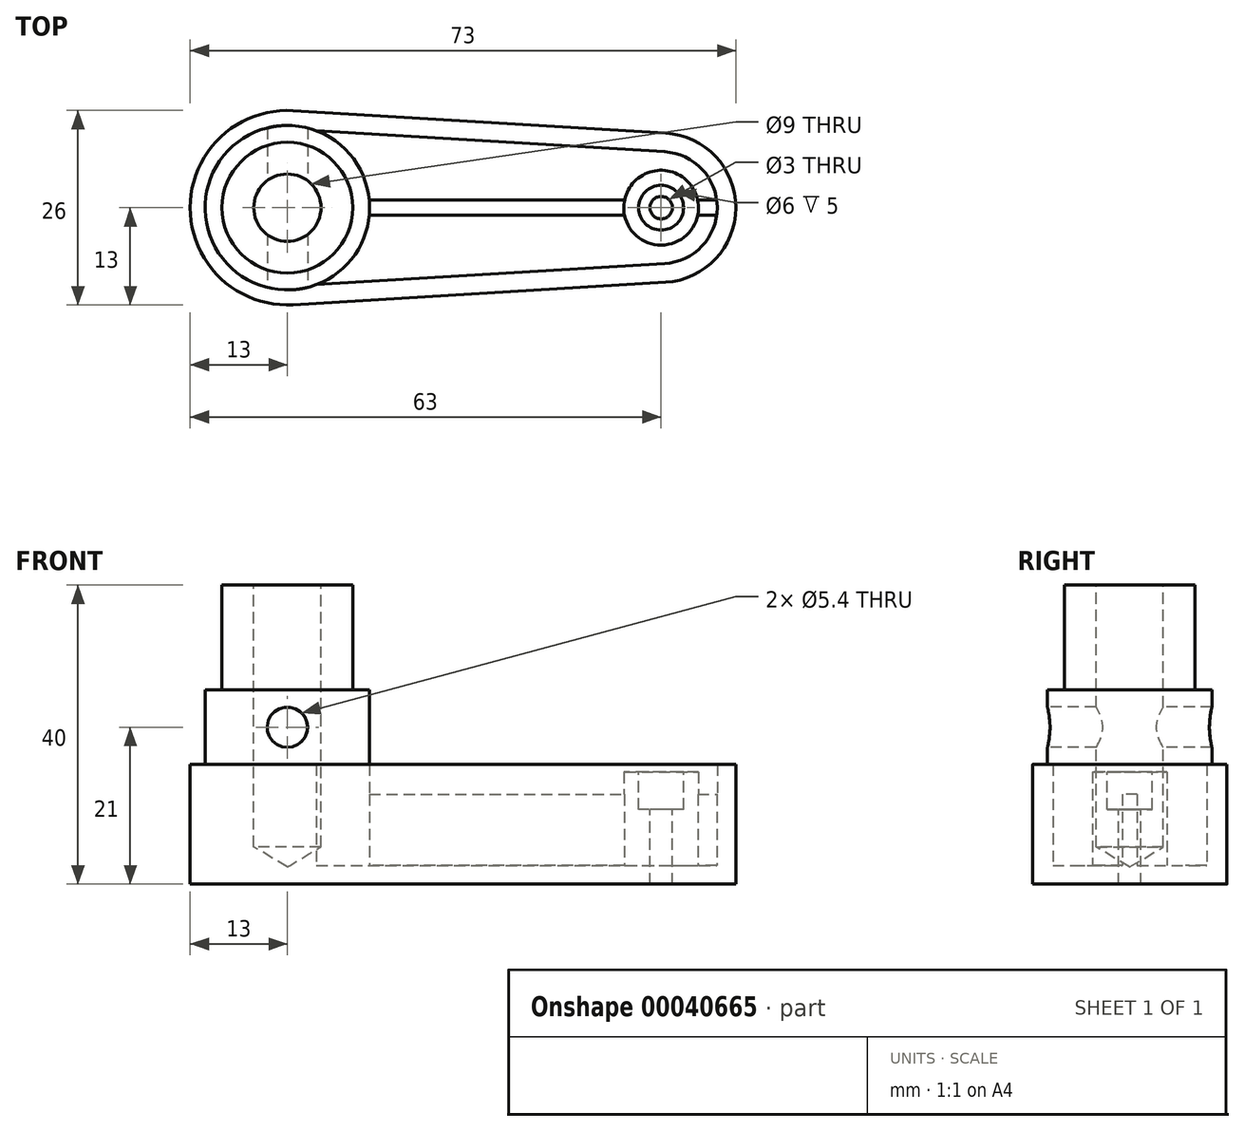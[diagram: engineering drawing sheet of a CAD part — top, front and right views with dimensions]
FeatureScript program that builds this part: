
annotation { "Feature Type Name" : "Feature", "Feature Type Description" : "" }
export const myFeature = defineFeature(function(context is Context, id is Id, definition is map)
    precondition{}
    {
        {
            var Q0;
            Q0=qCreatedBy(makeId("Top.planeOp"),FACE);
            var sketch = newSketch(context, id + "F0", { "sketchPlane" : qUnion([Q0])});
            skLineSegment(sketch, "E0", {"start": v(-11.49, 0) * mm, "end": v(64.24, 0) * mm, "construction": true});
            skLineSegment(sketch, "E1", {"start": v(0, -11.25) * mm, "end": v(0, 30.99) * mm, "construction": true});
            skLineSegment(sketch, "E2", {"start": v(50, -11.57) * mm, "end": v(50, 31.31) * mm, "construction": true});
            skCircle(sketch, "E3", {"center": v(0, 0) * mm, "radius": 13 * mm});
            skCircle(sketch, "E4", {"center": v(50, 0) * mm, "radius": 10 * mm});
            skLineSegment(sketch, "E5", {"start": v(0.78, 12.98) * mm, "end": v(50.6, 9.98) * mm});
            skLineSegment(sketch, "E6", {"start": v(0.78, -12.98) * mm, "end": v(50.6, -9.98) * mm});
            skSolve(sketch);
        }
        {
            var Q0;
            Q0=qSketchRegion(id+"F0",true);
            extrude(context, id + "F1", {"entities" : qUnion([Q0]), "depth" : 16 * mm});
        }
        {
            var Q0;
            Q0=makeQuery(id+"F1.opExtrude","CAP_FACE",FACE,{"disambiguationData":[OSD([sQuery(id+"F0.wireOp",EDGE,"E3"),sQuery(id+"F0.wireOp",EDGE,"E4"),sQuery(id+"F0.wireOp",EDGE,"E5"),sQuery(id+"F0.wireOp",EDGE,"E6")])],"isStart":false});
            shell(context, id + "F2", {"entities" : qUnion([Q0]), "thickness" : 2.5 * mm});
        }
        {
            var Q0;
            Q0=qCreatedBy(makeId("Top.planeOp"),FACE);
            var sketch = newSketch(context, id + "F3", { "sketchPlane" : qUnion([Q0])});
            skLineSegment(sketch, "E7.bottom", {"start": v(-12, 1) * mm, "end": v(58, 1) * mm});
            skLineSegment(sketch, "E7.top", {"start": v(-12, -1) * mm, "end": v(58, -1) * mm});
            skLineSegment(sketch, "E7.left", {"start": v(-12, 1) * mm, "end": v(-12, -1) * mm});
            skLineSegment(sketch, "E7.right", {"start": v(58, 1) * mm, "end": v(58, -1) * mm});
            skLineSegment(sketch, "E8", {"start": v(0, 0) * mm, "end": v(32, 0) * mm, "construction": true});
            skSolve(sketch);
        }
        {
            var Q0;
            Q0 = qSketchRegion(id + "F3", true);
            extrude(context, id + "F4", {"entities" : qUnion([Q0]), "operationType" : NewBodyOperationType.ADD, "depth" : 12 * mm});
        }
        {
            var Q0;
            Q0=qCreatedBy(makeId("Top.planeOp"),FACE);
            var sketch = newSketch(context, id + "F5", { "sketchPlane" : qUnion([Q0])});
            skCircle(sketch, "E9", {"center": v(50, 0) * mm, "radius": 5 * mm});
            skSolve(sketch);
        }
        {
            var Q0;
            Q0=qCreatedBy(makeId("Top.planeOp"),FACE);
            var sketch = newSketch(context, id + "F6", { "sketchPlane" : qUnion([Q0])});
            skCircle(sketch, "E10", {"center": v(0, 0) * mm, "radius": 11 * mm});
            skSolve(sketch);
        }
        {
            var Q0;
            Q0=qSketchRegion(id+"F6",true);
            extrude(context, id + "F7", {"entities" : qUnion([Q0]), "operationType" : NewBodyOperationType.ADD, "depth" : 26 * mm});
        }
        {
            var Q0;
            Q0=qCreatedBy(makeId("Top.planeOp"),FACE);
            var sketch = newSketch(context, id + "F8", { "sketchPlane" : qUnion([Q0])});
            skCircle(sketch, "E11", {"center": v(0, 0) * mm, "radius": 8.75 * mm});
            skSolve(sketch);
        }
        {
            var Q0;
            Q0 = qSketchRegion(id + "F5", true);
            extrude(context, id + "F9", {"entities" : qUnion([Q0]), "operationType" : NewBodyOperationType.ADD, "depth" : 15 * mm});
        }
        {
            var Q0;
            Q0=qSketchRegion(id+"F8",true);
            extrude(context, id + "F10", {"entities" : qUnion([Q0]), "operationType" : NewBodyOperationType.ADD, "depth" : 40 * mm});
        }
        {
            var Q0;
            Q0=makeQuery(id+"F10.opExtrude","CAP_FACE",FACE,{"disambiguationData":[OSD([sQuery(id+"F8.wireOp",EDGE,"E11")])],"isStart":false});
            var sketch = newSketch(context, id + "F11", { "sketchPlane" : qUnion([Q0])});
            skLineSegment(sketch, "E12", {"start": v(0, 0) * mm, "end": v(26.1, 0) * mm, "construction": true});
            skLineSegment(sketch, "E13", {"start": v(0, 0) * mm, "end": v(0, 20.1) * mm, "construction": true});
            skSolve(sketch);
        }
        {
            var Q0;
            Q0=sQuery(id+"F11.wireOp",VERTEX,"E12.start");
            var Q1;
            Q1=makeQuery(id+"F1.opExtrude","SWEPT_BODY",BODY,{"disambiguationData":[OSD([sQuery(id+"F0.wireOp",EDGE,"E3"),sQuery(id+"F0.wireOp",EDGE,"E4"),sQuery(id+"F0.wireOp",EDGE,"E5"),sQuery(id+"F0.wireOp",EDGE,"E6")])]});
            hole(context, id + "F12", {"style" : HoleStyle.SIMPLE, "holeDiameter" : 9 * mm, "endStyle" : HoleEndStyle.BLIND, "holeDepth" : 35 * mm, "locations" : qUnion([Q0]), "scope" : qUnion([Q1])});
        }
        {
            var Q0;
            Q0=qCreatedBy(makeId("Front.planeOp"),FACE);
            var sketch = newSketch(context, id + "F13", { "sketchPlane" : qUnion([Q0])});
            skLineSegment(sketch, "E14", {"start": v(0, 0) * mm, "end": v(0, 72.33) * mm, "construction": true});
            skLineSegment(sketch, "E15", {"start": v(-25.51, 21) * mm, "end": v(23.96, 21) * mm, "construction": true});
            skCircle(sketch, "E16", {"center": v(0, 21) * mm, "radius": 2.7 * mm});
            skSolve(sketch);
        }
        {
            var Q0;
            Q0=qSketchRegion(id+"F13",true);
            extrude(context, id + "F14", {"entities" : qUnion([Q0]), "operationType" : NewBodyOperationType.REMOVE, "endBound" : BoundingType.SYMMETRIC, "oppositeDirection" : true, "depth" : 25 * mm});
        }
        {
            var Q0;
            Q0=makeQuery(id+"F1.opExtrude","CAP_FACE",FACE,{"disambiguationData":[OSD([sQuery(id+"F0.wireOp",EDGE,"E3"),sQuery(id+"F0.wireOp",EDGE,"E4"),sQuery(id+"F0.wireOp",EDGE,"E5"),sQuery(id+"F0.wireOp",EDGE,"E6")])],"isStart":false});
            var sketch = newSketch(context, id + "F15", { "sketchPlane" : qUnion([Q0])});
            skLineSegment(sketch, "E17", {"start": v(50, 0) * mm, "end": v(73.03, 0) * mm, "construction": true});
            skPoint(sketch, "E17.endSnap0", {"position": v(60, 0) * mm});
            skLineSegment(sketch, "E18", {"start": v(50, 0) * mm, "end": v(50, 27.13) * mm, "construction": true});
            skSolve(sketch);
        }
        {
            var Q0;
            Q0=sQuery(id+"F15.wireOp",VERTEX,"E18.start");
            var Q1;
            Q1=makeQuery(id+"F1.opExtrude","SWEPT_BODY",BODY,{"disambiguationData":[OSD([sQuery(id+"F0.wireOp",EDGE,"E3"),sQuery(id+"F0.wireOp",EDGE,"E4"),sQuery(id+"F0.wireOp",EDGE,"E5"),sQuery(id+"F0.wireOp",EDGE,"E6")])]});
            hole(context, id + "F16", {"style" : HoleStyle.C_BORE, "holeDiameter" : 3 * mm, "cBoreDiameter" : 6 * mm, "cBoreDepth" : 5 * mm, "endStyle" : HoleEndStyle.THROUGH, "locations" : qUnion([Q0]), "scope" : qUnion([Q1])});
        }
    });
